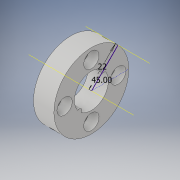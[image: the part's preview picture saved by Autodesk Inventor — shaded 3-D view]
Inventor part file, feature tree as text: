
AUTODESK INVENTOR PART (.ipt)
format: ipt  version: 2019 (Build 230136000, 136)  size: 168,960 bytes
history: native  units: in
note: dims shown in document units (in); Inventor stores cm internally (conversion verified against a paired STEP export)
features: sketch x5, extrude x4, plane x2, pattern_circular x1, mirror x1
ambient origin geometry x8: Origin, YZ Plane, XZ Plane, XY Plane, X Axis, Y Axis, Z Axis, Center Point
bodies: Solid1 (feature_tree)
feature tree (13):
  extrude  "Extrusion1"  Depth=1.7323in
  extrude  "Extrusion3"  Depth=1.2402in
  extrude  "Extrusion4"  Depth=1.1811in TaperAngle=0.0deg
  pattern_circular  "Circular Pattern1"  Count=4 Angle=360.0deg
  sketch  "Sketch6"  dims[d16=0.3937in d17=45.0deg]
  plane  "Work Plane1"
  extrude  "Extrusion5"  TaperAngle=45.0deg  [1 undecoded]
  plane  "Work Plane2"
  mirror  "Mirror1"
  sketch  "Sketch2"  dims[d3=0.7874in d4=1.7323in]
  sketch  "Sketch4"  dims[d5=0.4724in d6=0.0in d9=1.2402in]
  sketch  "Sketch5"  dims[d10=0.2008in d11=1.1811in d12=0.0in d13=1.5748in d14=360.0deg]
  sketch  "Sketch7"  dims[d18=0.1181in d19=45.0deg d20=0.3543in d21=0.2362in d22=0.0in d23=0.8661in d24=45.0deg d25=0.2047in d26=0.3937in d27=0.0in]
note: 1 required parameter value undecoded (feature->parameter linkage not recoverable at this tier; creation-order binding heuristic only, values carry confidence <= 0.55)
